# Revit family: Grohe_PlumbingFixture_BauContemporary_BathSpout_13252000a
name_source: partatom
category: Plumbing Fixtures
revit_build: Autodesk Revit 2016 (Build: 20150714_1515(x64)
units: mm (PartAtom-declared; Revit-internal decimal feet)

## family parameters
Cut with Voids When Loaded = No
Host = Face
OmniClass Number = 23.65.00.00
OmniClass Title = Supply and Distribution of Liquids and Gases
Part Type = Normal
Room Calculation Point = No
Round Connector Dimension = Use Diameter
Shared = No

## types (1)
- 13252000
    ADACompliant = No
    Assembly Code = C1030
    AssetType = Fixed
    BIMObjectName = Grohe_PlumbingFixture_BauContemporary_BathSpout_13252000
    ClassificationName = Uniclass2015
    ClassificationValue = Pr_40_20_87_96
    ColdWaterConnectionDiameter = 10 mm  [stored 0.0328084 ft]
    Color = Silver
    Cost = 0 $
    Default Elevation = 0 mm  [stored 0 ft]
    Description = wall mounted
 chrome finish
 mousseur
 projection 140 mm
 female thread 1/2"
    DurationUnit = Years
    Ecojoy = No
    ExpectedLife = 0
    Features = wall mounted
 chrome finish
 mousseur
 projection 140 mm
 female thread 1/2"
    Finish = Chrome
    HotWaterConnectionDiameter = 10 mm  [stored 0.0328084 ft]
    IfcExportAs = IfcPipeFitting
    IfcExportType = IfcPipeFittingType
    Keynote = N13
    LowEmittingMaterial = No
    Manufacturer = Grohe
    ManufacturerName = Grohe
    MasterformatNumber = 01 52 19
    MasterformatTitle = Sanitary Facilities
    Material = Chrome
    Model = GROHE BauContemporary Bath spout
    ModelNumber = 13252000
    ModelReference = GROHE BauContemporary Bath spout
    NBSDescription = Water supply fittings for wash basins and troughs
    NBSObjectName = Grohe - Water supply fittings for wash basins and troughs
    NBSReference = 45-35-70/371
    NominalDepth = 0 mm  [stored 0 ft]
    NominalHeight = 0 mm  [stored 0 ft]
    NominalLength = 0 mm  [stored 0 ft]
    ProductDocumentationLink = https://www.grohe.nz
    ProductPageURL = https://www.grohe.nz
    ProductionYear = 2018
    Type Comments = 13252000
    TypeName = GROHE BauContemporary Bath spout
    URL = https://www.grohe.co.uk
    WarrantyDurationLabor = 0
    WarrantyDurationParts = 0
    WarrantyDurationUnit = Years
    _BSBibleVersion = 15
    _BimSpecGuid = 0
    _CurrentRevision = 1
    _DistributedBy = www.bimstore.co.uk

note: [stored X ft] marks values corroborated as IEEE doubles in the binary element streams (Revit-internal decimal feet)

## geometry (parser evidence)
native form markers: Blend x2, Sweep x2
no freeform markers — native parametric forms only
